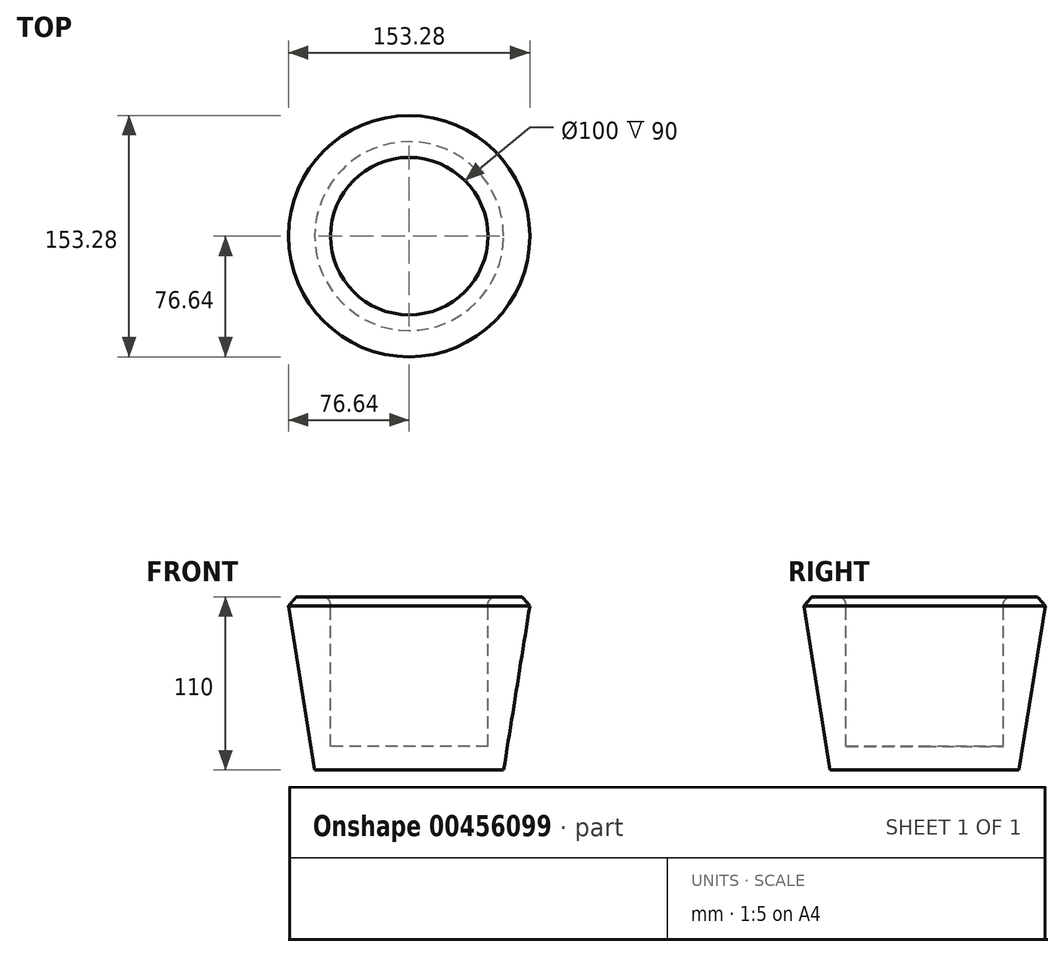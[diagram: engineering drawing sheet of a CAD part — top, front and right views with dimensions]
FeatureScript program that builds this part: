
annotation { "Feature Type Name" : "Feature", "Feature Type Description" : "" }
export const myFeature = defineFeature(function(context is Context, id is Id, definition is map)
    precondition{}
    {
        {
            var Q0;
            Q0=qCreatedBy(makeId("Front.planeOp"),FACE);
            var sketch = newSketch(context, id + "F0", { "sketchPlane" : qUnion([Q0])});
            skLineSegment(sketch, "E0", {"start": v(0, 88.05) * mm, "end": v(0, -97.32) * mm, "construction": true});
            skLineSegment(sketch, "E1", {"start": v(0, 0) * mm, "end": v(-60, 0) * mm});
            skLineSegment(sketch, "E2", {"start": v(-60, 0) * mm, "end": v(-77.56, 110) * mm});
            skLineSegment(sketch, "E3", {"start": v(-50, 110) * mm, "end": v(-50, 15) * mm});
            skLineSegment(sketch, "E4", {"start": v(-50, 15) * mm, "end": v(0, 15) * mm});
            skLineSegment(sketch, "E5", {"start": v(0, 15) * mm, "end": v(0, 0) * mm});
            skLineSegment(sketch, "E6", {"start": v(-77.56, 110) * mm, "end": v(-50, 110) * mm});
            skSolve(sketch);
        }
        {
            var Q0;
            Q0 = qSketchRegion(id + "F0", true);
            var Q1;
            Q1=sQuery(id+"F0.wireOp",EDGE,"E0");
            revolve(context, id + "F1", {"entities" : qUnion([Q0]), "axis" : qUnion([Q1]), "revolveType" : RevolveType.FULL});
        }
        {
            var Q0;
            Q0=makeQuery(id+"F1.opRevolve","SWEPT_EDGE",EDGE,{"disambiguationData":[OSD([sQuery(id+"F0.wireOp",EDGE,"E3"),sQuery(id+"F0.wireOp",EDGE,"E6")])]});
            fillet(context, id + "F2", {"entities" : qUnion([Q0]), "radius" : 5 * mm, "tangentPropagation" : true, "allowEdgeOverflow" : false});
        }
        {
            var Q0;
            Q0=makeQuery(id+"F1.opRevolve","SWEPT_EDGE",EDGE,{"disambiguationData":[OSD([sQuery(id+"F0.wireOp",EDGE,"E2"),sQuery(id+"F0.wireOp",EDGE,"E6")])]});
            chamfer(context, id + "F3", {"entities" : qUnion([Q0]), "width" : 5 * mm, "tangentPropagation" : true});
        }
        {
            var Q0;
            {var subQ0=sQuery(id+"F0.wireOp",EDGE,"E6");Q0=makeQuery(id+"F3.opChamfer","BLEND_EDGE",EDGE,{"blendedFrom":[makeQuery(id+"F1.opRevolve","SWEPT_EDGE",EDGE,{"disambiguationData":[OSD([sQuery(id+"F0.wireOp",EDGE,"E2"),subQ0])]}),makeQuery(id+"F1.opRevolve","SWEPT_FACE",FACE,{"disambiguationData":[OSD([subQ0])]})],"blendedInto":[makeQuery(id+"F1.opRevolve","SWEPT_FACE",FACE,{"disambiguationData":[OSD([subQ0])]})]});}
            fillet(context, id + "F4", {"entities" : qUnion([Q0]), "radius" : 1.5 * mm, "tangentPropagation" : true, "allowEdgeOverflow" : false});
        }
    });
